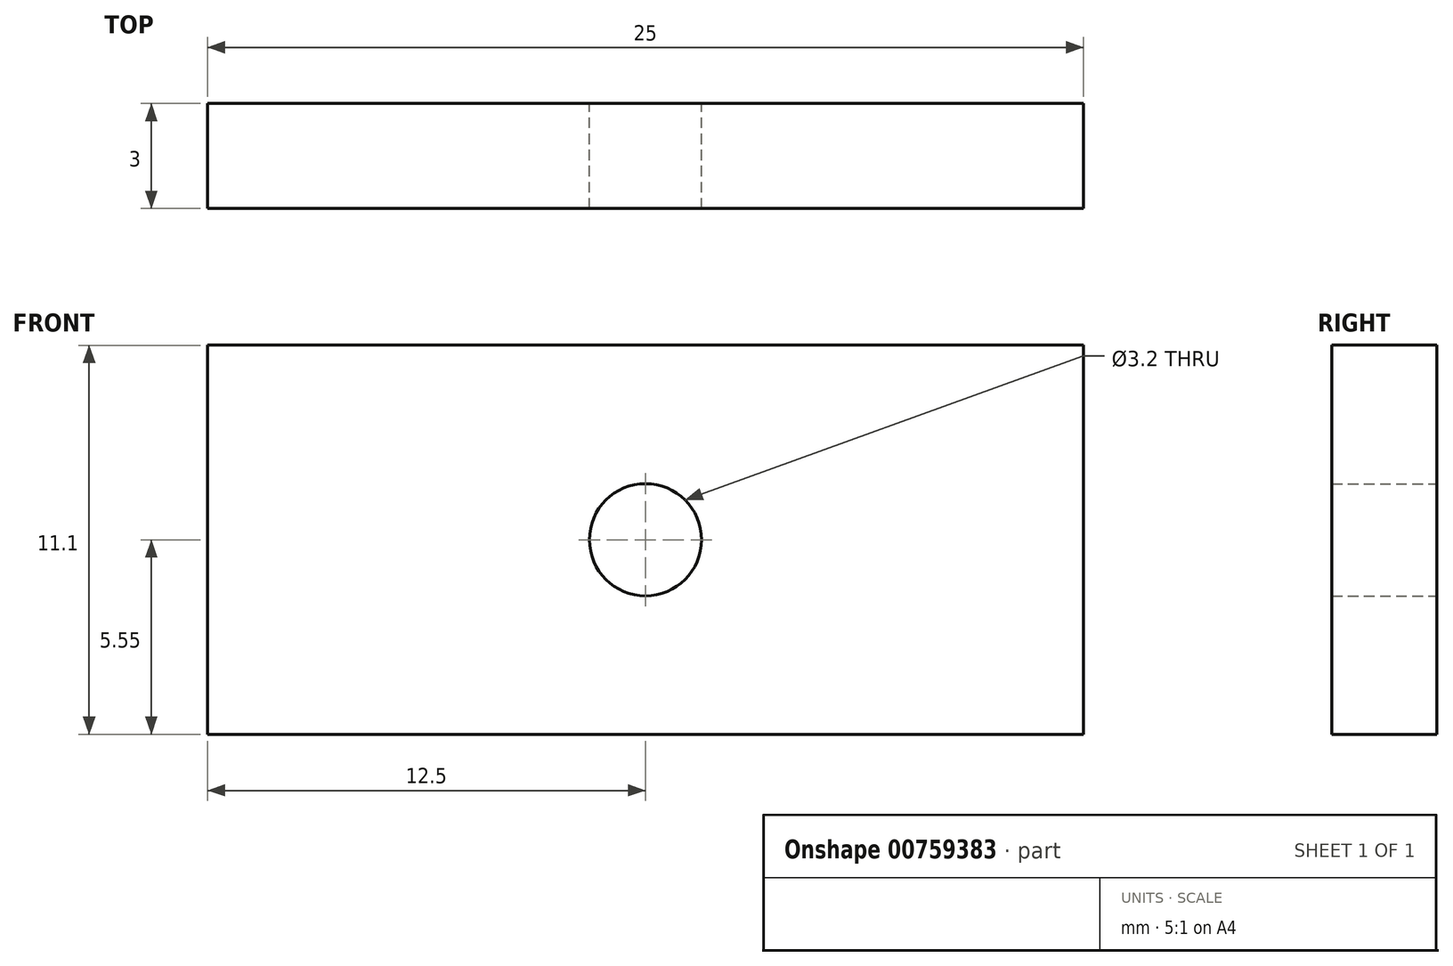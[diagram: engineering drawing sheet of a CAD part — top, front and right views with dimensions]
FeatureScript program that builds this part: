
annotation { "Feature Type Name" : "Feature", "Feature Type Description" : "" }
export const myFeature = defineFeature(function(context is Context, id is Id, definition is map)
    precondition{}
    {
        {
            var Q0;
            Q0=qCreatedBy(makeId("Front.planeOp"),FACE);
            var sketch = newSketch(context, id + "F0", { "sketchPlane" : qUnion([Q0])});
            skLineSegment(sketch, "E0.bottom", {"start": v(12.5, -5.55) * mm, "end": v(-12.5, -5.56) * mm});
            skLineSegment(sketch, "E0.top", {"start": v(12.5, 5.56) * mm, "end": v(-12.5, 5.55) * mm});
            skLineSegment(sketch, "E0.left", {"start": v(12.5, -5.55) * mm, "end": v(12.5, 5.56) * mm});
            skLineSegment(sketch, "E0.right", {"start": v(-12.5, -5.56) * mm, "end": v(-12.5, 5.55) * mm});
            skPoint(sketch, "E0.middle", {"position": v(0, 0) * mm});
            skCircle(sketch, "E1", {"center": v(0, 0) * mm, "radius": 1.6 * mm});
            skSolve(sketch);
        }
        {
            var Q0;
            Q0=makeQuery(id+"F0.imprint","IMPRINT",FACE,{"disambiguationData":[TD([[makeQuery(id+"F0.imprint","IMPRINT",EDGE,{"derivedFrom":sQuery(id+"F0.wireOp",EDGE,"E0.bottom")}),-1.0]])]});
            extrude(context, id + "F1", {"entities" : qUnion([Q0]), "depth" : 3 * mm, "offsetDistance" : 25 * mm});
        }
    });
